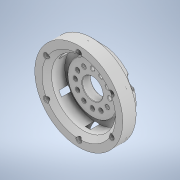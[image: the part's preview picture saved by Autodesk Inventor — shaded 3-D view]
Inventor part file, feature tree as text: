
AUTODESK INVENTOR PART (.ipt)
format: ipt  version: 2020 (Build 240168000, 168)  size: 485,888 bytes
history: native  units: in
note: dims shown in document units (in); Inventor stores cm internally (conversion verified against a paired STEP export)
features: extrude x8, sketch x8, chamfer x3, plane x1, projected_geometry x1
ambient origin geometry x8: Origin, YZ Plane, XZ Plane, XY Plane, X Axis, Y Axis, Z Axis, Center Point
bodies: Solid1 (feature_tree)
feature tree (21):
  extrude  "Extrusion1"  Depth=1.23in TaperAngle=0.0deg
  extrude  "Extrusion2"  Depth=3.51in
  extrude  "Extrusion3"  Depth=0.75in TaperAngle=0.0deg
  chamfer  "Chamfer1"  Distance=0.5in Angle=45.0deg
  plane  "Work Plane1"
  extrude  "Extrusion4"  Depth=2.0625in
  extrude  "Extrusion5"  Depth=0.2656in
  extrude  "Extrusion6"  TaperAngle=0.0deg  [1 undecoded]
  chamfer  "Chamfer2"  Distance=2.3622in Angle=360.0deg
  extrude  "Extrusion7"  Depth=0.2031in
  extrude  "Extrusion8"  Depth=0.9375in
  chamfer  "Chamfer3"  Distance=4.7244in Angle=360.0deg
  sketch  "Sketch1"  dims[d0=4.825in d1=1.23in d2=0.0in]
  sketch  "Sketch2"  dims[d3=2.74in d4=3.51in]
  sketch  "Sketch3"  dims[d5=0.99in d6=0.0in d7=0.75in d8=0.0in d9=0.5in d10=0.125in d11=45.0deg]
  projected_geometry  "Projected Loop1"
  sketch  "Sketch5"  dims[d12=-0.5in d13=2.0625in]
  sketch  "Sketch6"  dims[d14=2.3622in d16=360.0deg d18=0.2656in]
  sketch  "Sketch8"  dims[d19=0.5in d20=0.0in d26=0.0in d27=0.0in]
  sketch  "Sketch9"  dims[d28=0.69in d29=2.3622in d31=360.0deg]
  sketch  "Sketch10"  dims[d33=1.126in d34=0.2031in d35=0.9375in d36=4.7244in d38=360.0deg d40=0.0in d41=0.0in d42=0.025in d43=0.125in d44=45.0deg d45=2.3622in d47=360.0deg d49=0.0118in d50=0.0in d51=2.3622in d53=360.0deg d55=0.0118in d56=0.0in d57=0.26in d58=0.125in d59=45.0deg]
note: 1 required parameter value undecoded (feature->parameter linkage not recoverable at this tier; creation-order binding heuristic only, values carry confidence <= 0.55)
